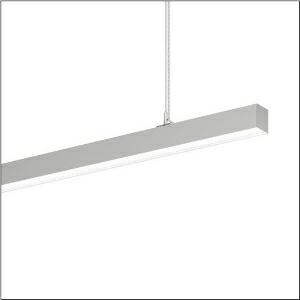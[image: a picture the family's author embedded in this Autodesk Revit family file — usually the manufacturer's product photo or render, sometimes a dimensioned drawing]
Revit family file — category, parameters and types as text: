
# Revit family: silica_r__21_51mx30db45sb_ca73
name_source: partatom
category: Lighting Fixtures
units: mm (PartAtom-declared; Revit-internal decimal feet)

## family parameters
Cut with Voids When Loaded = No
Host = Face
Light Source = No
Part Type = Normal
Room Calculation Point = No
Round Connector Dimension = Use Diameter
Shared = No

## types (1)
- --- (1 x LED, 5260 lm, 32 W, 4000K)
    Apparent Load = 32 VA
    CIE Flux Codes = 47 79 96 57 100
    Color Rendering = 80
    Color Temperature = 4000K
    Default Elevation = 1800 mm
    Description = Silica® 21, office luminaire, primary optical cover: cover, of PMMA, opal, light emission: direct/indirect distribution, primary light characteristic: symmetric, installation type: suspended mounting, LED, rated luminous flux: 5.260lm, luminous efficacy: 164lm/W, light colour: 840, colour temperature: 4000K, control gear: DALI 2, with terminal, 3+2-pole, max. 2.5mm², mains connection: 220..240V, AC, 50/60Hz, rated input power: 32W, luminaire housing, of aluminium, metallic grey (RAL 9006), length: 1.504mm, width: 53mm, height: 53mm, protection rating (complete): IP20, insulation class (complete): insulation class I (protective earthing), certification: CE, permissible operating ambient temperature: 0..+35°C, standard: EN 50419, packaging unit: 1 piece
    Height = 53 mm
    Lamp = 1 x LED
    Lamp Light Flux = 5260 lm
    Lamp Power = 32 W
    Lamp count = 1
    Length = 1504 mm
    Luminous efficacy = 164 lm/W
    Manufacturer = Siteco
    ModVariant = No
    Model = 51MX30DB45SB
    Mounting Place = Ceiling
    Mounting Type = Pendant
    Number of Poles = 1
    OnlyDefault = Yes
    Power Factor = 1
    Product Name = Silica® 21
    Product group = office luminaire | ceiling pendant
    ProductGroupID = 904
    Protection Class = Protection class I
    Protection Degree = IP 20
    RLX_Detail_Level = 1
    RLX_Emergency_Light_Flux = 0 lm
    RLX_Emergency_Type = 0
    RLX_Emergency_Type_DB = No
    RlxData = <blob elided: 23325 chars, md5=b88e2023>
    Socket = socket
    Standby Power = 0 W
    System Light Flux = 5260 lm
    System Power = 32 W
    Type Comments = factory setting: luminous flux: 100 % | dim-lin: 254 | 218 mA
    Type Image = l_1335864.jpg
    URL = http://relux.com
    VarID = @adj_116936
    Voltage = 0 V
    Weight = 0.00 kg
    Width = 53 mm

## geometry (parser evidence)
native form markers: Blend x4, Sweep x12
no freeform markers — native parametric forms only
